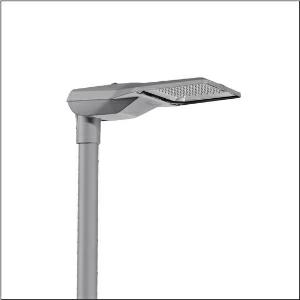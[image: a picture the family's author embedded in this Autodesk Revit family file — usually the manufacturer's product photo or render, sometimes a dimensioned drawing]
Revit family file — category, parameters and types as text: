
# Revit family: streetlight_sl_21_midi___st0_8a_5xe3c33s08nb_db16
name_source: partatom
category: Lighting Fixtures
units: mm (PartAtom-declared; Revit-internal decimal feet)

## family parameters
Cut with Voids When Loaded = No
Host = Face
Light Source = No
Part Type = Normal
Room Calculation Point = No
Round Connector Dimension = Use Diameter
Shared = No

## types (1)
- --- (1 x LED, 22700 lm, 151.2 W, 3000K)
    Apparent Load = 151 VA
    CIE Flux Codes = 41 75 97 100 100
    Color Rendering = 70
    Color Temperature = 3000K
    Default Elevation = 1800 mm
    Description = Streetlight SL 21 midi, mast luminaire, primary light control with lens, of PMMA, primary optical cover: cover, of toughened safety glass, transparent, light distribution: ST0.8a, light emission: direct distribution, primary light characteristic: asymmetric, installation type: side-entry, post-top, LED, High Power LED, rated luminous flux: 22.700lm, luminous efficacy: 150lm/W, light colour: 730, colour temperature: 3000K, control: overheat protection, constant luminous flux control, time-dependent luminous flux control, flexible luminous flux parameterisation, presetting dimming logarithmic, mains connection: 230..240V, AC, 50/60Hz, start of lifetime: 151W, end of service life: 157W, reduction: 70W, luminaire housing, of diecast aluminium, powder-coated, Siteco® metallic grey (DB 702S), corrosivity category C5 mid according to DIN EN ISO 12944, please order mast flange separately, inclination adjustable: 0°, 5°, 10°, 15°, sealing non-destructively replaceable, multi-level sealing system, length: 644mm, width: 335mm, height: 110mm, mast flange for spigot size: 42mm (side-entry): 5XC10008XM4, 60/48mm (side-entry/post-top): 5XC10108XM2, 76/60mm (side-entry/post-top): 5XC10108XM1, Smart Interface above, protection rating (complete): IP66, insulation class (complete): insulation class II (safety insulation), certification: CE, ENEC, ENEC+, VDE, impact resistance: IK09, permissible operating ambient temperature for outdoor applications: -40..+50°C, standard-compliant lighting for roads and squares, packaging unit: 1 piece

Light Distribution: ST0.8a
    Height = 111 mm
    Lamp = 1 x LED
    Lamp Light Flux = 22700 lm
    Lamp Power = 151.2 W
    Lamp count = 1
    Length = 644 mm
    Luminous efficacy = 150 lm/W
    Manufacturer = Siteco
    ModVariant = No
    Model = 5XE3C33S08NB
    Number of Poles = 1
    OnlyDefault = Yes
    Power Factor = 1
    Product Name = Streetlight SL 21 midi | ST0.8a
    Product group = mast luminaire | pylon top
    ProductGroupID = 6100
    Protection Class = Protection class II
    Protection Degree = IP 66
    RLX_Detail_Level = 1
    RLX_Emergency_Light_Flux = 0 lm
    RLX_Emergency_Type = 0
    RLX_Emergency_Type_DB = No
    RlxData = <blob elided: 91161 chars, md5=205c39ea>
    Socket = socket
    Standby Power = 0 W
    System Light Flux = 22700 lm
    System Power = 151 W
    Type Comments = factory setting: luminous flux: 100 % | dim-lin: 254 | 802 mA
    Type Image = l_1004302.jpg
    URL = http://relux.com
    VarID = @adj_101187
    Voltage = 0 V
    Weight = 0.00 kg
    Width = 336 mm

## geometry (parser evidence)
native form markers: Blend x4, Sweep x9
no freeform markers — native parametric forms only
